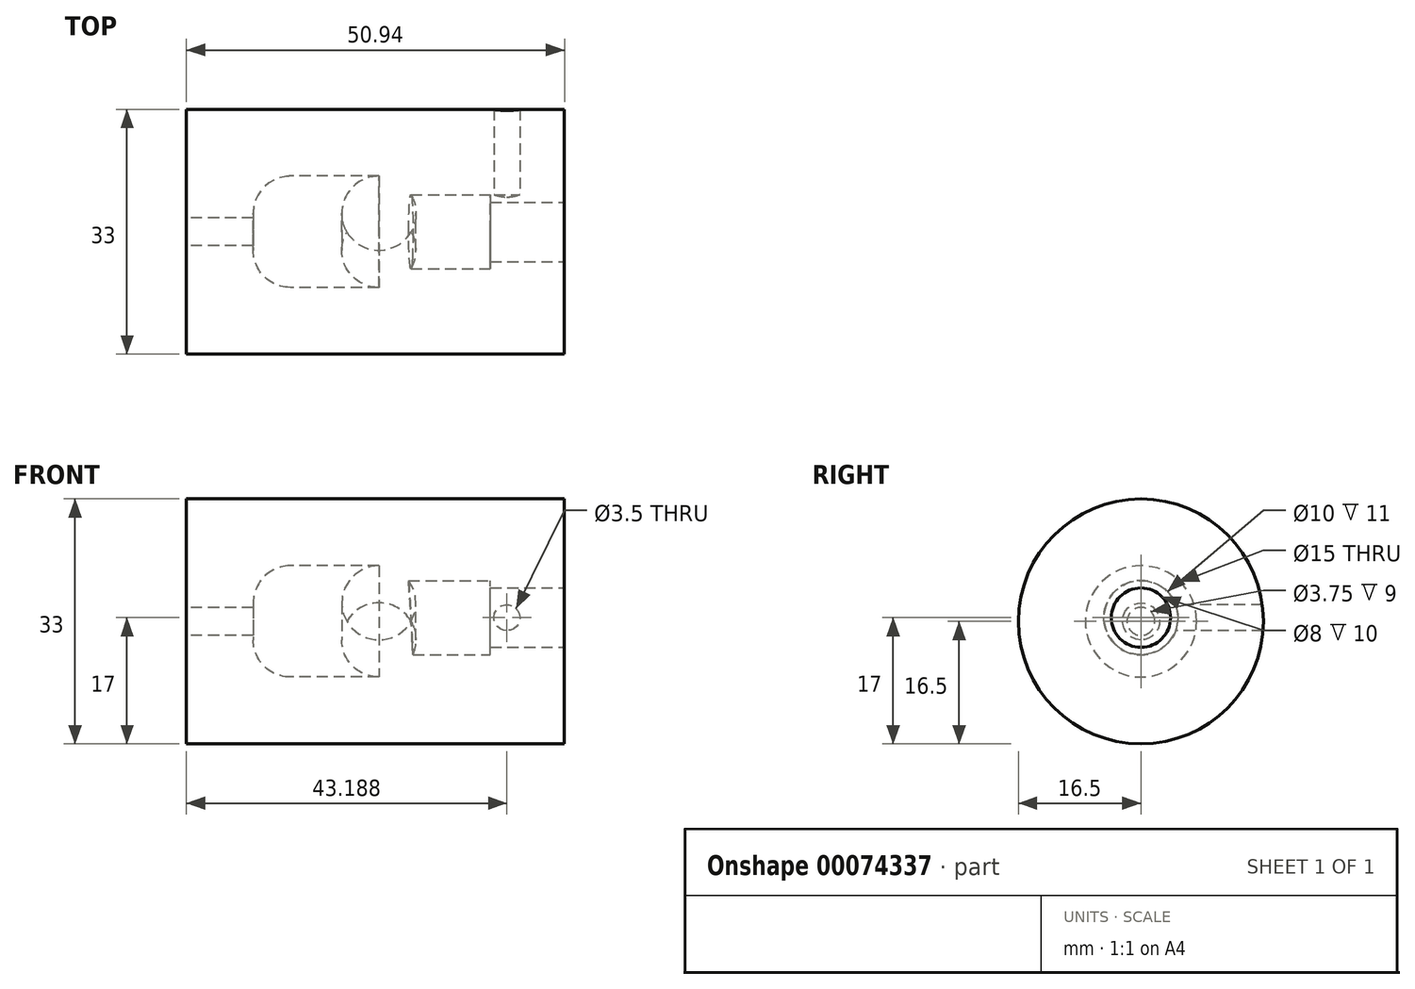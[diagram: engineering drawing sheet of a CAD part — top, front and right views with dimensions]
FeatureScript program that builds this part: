
annotation { "Feature Type Name" : "Feature", "Feature Type Description" : "" }
export const myFeature = defineFeature(function(context is Context, id is Id, definition is map)
    precondition{}
    {
        {
            var Q0;
            Q0=qCreatedBy(makeId("Front.planeOp"),FACE);
            var sketch = newSketch(context, id + "F0", { "sketchPlane" : qUnion([Q0])});
            skLineSegment(sketch, "E0", {"start": v(0, 0) * mm, "end": v(32.03, 0) * mm});
            skLineSegment(sketch, "E1.bottom", {"start": v(0, 1.88) * mm, "end": v(9, 1.88) * mm});
            skLineSegment(sketch, "E1.top", {"start": v(0, 16.5) * mm, "end": v(9, 16.5) * mm});
            skLineSegment(sketch, "E1.left", {"start": v(0, 1.88) * mm, "end": v(0, 16.5) * mm});
            skLineSegment(sketch, "E1.right", {"start": v(9, 1.87) * mm, "end": v(9, 2.5) * mm});
            skLineSegment(sketch, "E2.bottom", {"start": v(9, 16.5) * mm, "end": v(30.94, 16.5) * mm});
            skLineSegment(sketch, "E2.top", {"start": v(14, 7.5) * mm, "end": v(25.94, 7.5) * mm});
            skLineSegment(sketch, "E2.left", {"start": v(9, 16.5) * mm, "end": v(9, 7.5) * mm});
            skLineSegment(sketch, "E2.right", {"start": v(30.94, 16.5) * mm, "end": v(30.94, 7.5) * mm});
            skLineSegment(sketch, "E3.bottom", {"start": v(30.94, 16.5) * mm, "end": v(50.94, 16.5) * mm});
            skLineSegment(sketch, "E3.top", {"start": v(30.94, 0) * mm, "end": v(50.94, 0) * mm});
            skLineSegment(sketch, "E3.left", {"start": v(30.94, 2.5) * mm, "end": v(30.94, 0) * mm});
            skLineSegment(sketch, "E3.right", {"start": v(50.94, 16.5) * mm, "end": v(50.94, 0) * mm});
            skLineSegment(sketch, "E4.MirrorCS", {"start": v(30.94, -16.5) * mm, "end": v(50.94, -16.5) * mm});
            skLineSegment(sketch, "E5.MirrorCS", {"start": v(0, -1.88) * mm, "end": v(9, -1.88) * mm});
            skLineSegment(sketch, "E6.MirrorCS", {"start": v(0, -16.5) * mm, "end": v(9, -16.5) * mm});
            skLineSegment(sketch, "E7.MirrorCS", {"start": v(0, -1.88) * mm, "end": v(0, -16.5) * mm});
            skLineSegment(sketch, "E8.MirrorCS", {"start": v(30.94, -16.5) * mm, "end": v(30.94, -7.5) * mm});
            skLineSegment(sketch, "E9.MirrorCS", {"start": v(9, -16.5) * mm, "end": v(9, -7.5) * mm});
            skLineSegment(sketch, "E10.MirrorCS", {"start": v(14, -7.5) * mm, "end": v(25.94, -7.5) * mm});
            skLineSegment(sketch, "E11.MirrorCS", {"start": v(9, -16.5) * mm, "end": v(30.94, -16.5) * mm});
            skLineSegment(sketch, "E12.MirrorCS", {"start": v(9, -1.87) * mm, "end": v(9, -2.5) * mm});
            skLineSegment(sketch, "E13.MirrorCS", {"start": v(30.94, -2.5) * mm, "end": v(30.94, 0) * mm});
            skLineSegment(sketch, "E14.MirrorCS", {"start": v(50.94, -16.5) * mm, "end": v(50.94, 0) * mm});
            skPoint(sketch, "E15.newPointA", {"position": v(9, 16.5) * mm});
            skPoint(sketch, "E15.newPointB", {"position": v(9, 7.5) * mm});
            skArc(sketch, "E15.filletArc", {"start": v(14, 7.5) * mm, "mid": v(10.46, 6.04) * mm, "end": v(9, 2.5) * mm});
            skPoint(sketch, "E16.newPointA", {"position": v(30.94, 7.5) * mm});
            skPoint(sketch, "E16.newPointB", {"position": v(30.94, 16.5) * mm});
            skArc(sketch, "E16.filletArc", {"start": v(30.94, 2.5) * mm, "mid": v(29.47, 6.04) * mm, "end": v(25.94, 7.5) * mm});
            skPoint(sketch, "E17.newPointA", {"position": v(30.94, -16.5) * mm});
            skPoint(sketch, "E17.newPointB", {"position": v(30.94, -7.5) * mm});
            skArc(sketch, "E17.filletArc", {"start": v(25.94, -7.5) * mm, "mid": v(29.47, -6.04) * mm, "end": v(30.94, -2.5) * mm});
            skPoint(sketch, "E18.newPointA", {"position": v(9, -16.5) * mm});
            skPoint(sketch, "E18.newPointB", {"position": v(9, -7.5) * mm});
            skArc(sketch, "E18.filletArc", {"start": v(9, -2.5) * mm, "mid": v(10.46, -6.04) * mm, "end": v(14, -7.5) * mm});
            skSolve(sketch);
        }
        {
            var Q0;
            Q0=makeQuery(id+"F0.imprint","IMPRINT",FACE,{"disambiguationData":[TD([[makeQuery(id+"F0.imprint","IMPRINT",EDGE,{"derivedFrom":sQuery(id+"F0.wireOp",EDGE,"E1.bottom")}),1.0]])]});
            var Q1;
            {var subQ0=sQuery(id+"F0.wireOp",EDGE,"E2.bottom");Q1=makeQuery(id+"F0.imprint","IMPRINT",FACE,{"disambiguationData":[TD([[makeQuery(id+"F0.imprint","IMPRINT",EDGE,{"derivedFrom":subQ0}),-1.0]])]});}
            var Q2;
            {var subQ5=sQuery(id+"F0.wireOp",EDGE,"E3.bottom");Q2=makeQuery(id+"F0.imprint","IMPRINT",FACE,{"disambiguationData":[TD([[makeQuery(id+"F0.imprint","IMPRINT",EDGE,{"derivedFrom":subQ5}),-1.0]])]});}
            var Q3;
            Q3=sQuery(id+"F0.wireOp",EDGE,"E0");
            revolve(context, id + "F1", {"entities" : qUnion([Q0, Q1, Q2]), "axis" : qUnion([Q3]), "revolveType" : RevolveType.FULL});
        }
        {
            var Q0;
            Q0=makeQuery(id+"F1.opRevolve","SWEPT_FACE",FACE,{"disambiguationData":[OSD([sQuery(id+"F0.wireOp",EDGE,"E3.right")])]});
            var sketch = newSketch(context, id + "F2", { "sketchPlane" : qUnion([Q0])});
            skCircle(sketch, "E19", {"center": v(0, 0.5) * mm, "radius": 4 * mm});
            skCircle(sketch, "E20", {"center": v(0, 0.5) * mm, "radius": 5 * mm});
            skSolve(sketch);
        }
        {
            var Q0;
            Q0=makeQuery(id+"F2.imprint","IMPRINT",FACE,{"disambiguationData":[TD([[makeQuery(id+"F2.imprint","IMPRINT",EDGE,{"derivedFrom":sQuery(id+"F2.wireOp",EDGE,"E19")}),1.0]])]});
            extrude(context, id + "F3", {"entities" : qUnion([Q0]), "operationType" : NewBodyOperationType.REMOVE, "endBound" : BoundingType.UP_TO_NEXT, "oppositeDirection" : true, "depth" : 25 * mm});
        }
        {
            var Q0;
            Q0=qCreatedBy(makeId("Front.planeOp"),FACE);
            var sketch = newSketch(context, id + "F4", { "sketchPlane" : qUnion([Q0])});
            skCircle(sketch, "E21", {"center": v(43.19, 0.5) * mm, "radius": 1.75 * mm});
            skSolve(sketch);
        }
        {
            var Q0;
            Q0 = qSketchRegion(id + "F4", true);
            extrude(context, id + "F5", {"entities" : qUnion([Q0]), "operationType" : NewBodyOperationType.REMOVE, "oppositeDirection" : true, "depth" : 25 * mm});
        }
        {
            var Q0;
            Q0 = qSketchRegion(id + "F2", true);
            extrude(context, id + "F6", {"entities" : qUnion([Q0]), "operationType" : NewBodyOperationType.REMOVE, "oppositeDirection" : true, "depth" : 25 * mm});
        }
        {
            var Q0;
            Q0 = qSketchRegion(id + "F2", true);
            extrude(context, id + "F7", {"entities" : qUnion([Q0]), "operationType" : NewBodyOperationType.ADD, "oppositeDirection" : true, "depth" : 10 * mm});
        }
    });
